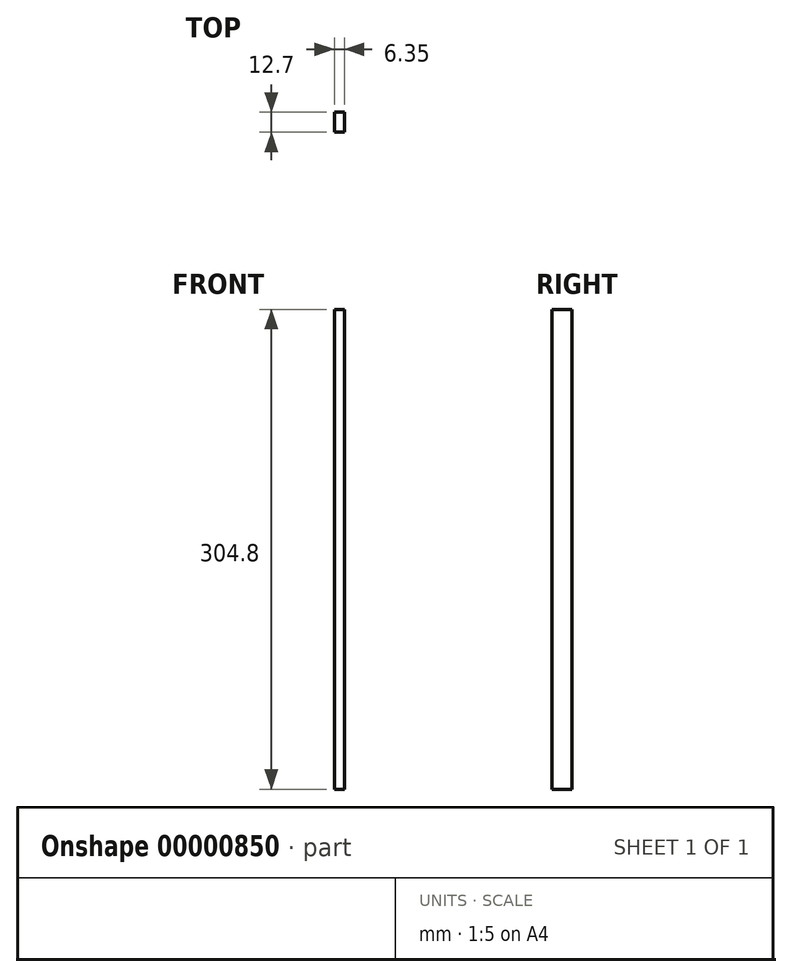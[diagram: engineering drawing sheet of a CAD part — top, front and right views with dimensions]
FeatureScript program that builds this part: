
annotation { "Feature Type Name" : "Feature", "Feature Type Description" : "" }
export const myFeature = defineFeature(function(context is Context, id is Id, definition is map)
    precondition{}
    {
        {
            var Q0;
            Q0=qCreatedBy(makeId("Right.planeOp"),FACE);
            var sketch = newSketch(context, id + "F0", { "sketchPlane" : qUnion([Q0])});
            skLineSegment(sketch, "E0", {"start": v(0, 430.16) * mm, "end": v(0, -453.51) * mm, "construction": true});
            skLineSegment(sketch, "E1", {"start": v(-808.7, 0) * mm, "end": v(843.12, 0) * mm, "construction": true});
            skLineSegment(sketch, "E2.bottom", {"start": v(-6.35, 0) * mm, "end": v(6.35, 0) * mm});
            skLineSegment(sketch, "E2.top", {"start": v(-6.35, 304.8) * mm, "end": v(6.35, 304.8) * mm});
            skLineSegment(sketch, "E2.left", {"start": v(-6.35, 0) * mm, "end": v(-6.35, 304.8) * mm});
            skLineSegment(sketch, "E2.right", {"start": v(6.35, 0) * mm, "end": v(6.35, 304.8) * mm});
            skSolve(sketch);
        }
        {
            var Q0;
            Q0=qSketchRegion(id+"F0",true);
            extrude(context, id + "F1", {"entities" : qUnion([Q0]), "oppositeDirection" : true, "depth" : 6.35 * mm});
        }
    });
